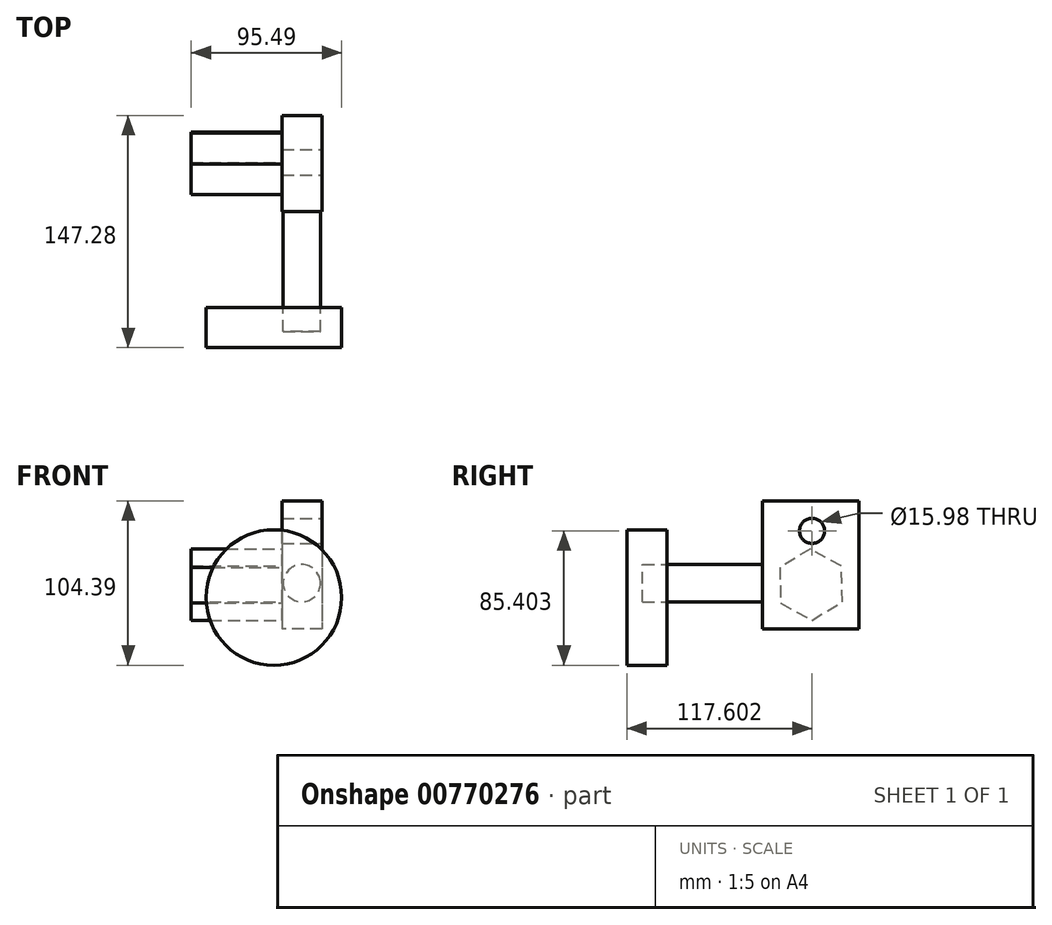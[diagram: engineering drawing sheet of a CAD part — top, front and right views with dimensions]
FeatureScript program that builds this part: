
annotation { "Feature Type Name" : "Feature", "Feature Type Description" : "" }
export const myFeature = defineFeature(function(context is Context, id is Id, definition is map)
    precondition{}
    {
        {
            var Q0;
            Q0=qCreatedBy(makeId("Front.planeOp"),FACE);
            var sketch = newSketch(context, id + "F0", { "sketchPlane" : qUnion([Q0])});
            skCircle(sketch, "E0", {"center": v(-5.26, 6.11) * mm, "radius": 43.06 * mm});
            skSolve(sketch);
        }
        {
            var Q0;
            Q0=makeQuery(id+"F0.imprint","IMPRINT",FACE,{"disambiguationData":[TD([[makeQuery(id+"F0.imprint","IMPRINT",EDGE,{"derivedFrom":sQuery(id+"F0.wireOp",EDGE,"E0")}),1.0]])]});
            extrude(context, id + "F1", {"entities" : qUnion([Q0]), "depth" : 25.4 * mm, "offsetDistance" : 25.4 * mm});
        }
        {
            var Q0;
            Q0=qCreatedBy(makeId("Right.planeOp"),FACE);
            var sketch = newSketch(context, id + "F2", { "sketchPlane" : qUnion([Q0])});
            skLineSegment(sketch, "E1.bottom", {"start": v(60.8, 67.44) * mm, "end": v(121.88, 67.44) * mm});
            skLineSegment(sketch, "E1.top", {"start": v(60.8, -13.97) * mm, "end": v(121.88, -13.97) * mm});
            skLineSegment(sketch, "E1.left", {"start": v(60.8, 67.44) * mm, "end": v(60.8, -13.97) * mm});
            skLineSegment(sketch, "E1.right", {"start": v(121.88, 67.44) * mm, "end": v(121.88, -13.97) * mm});
            skSolve(sketch);
        }
        {
            var Q0;
            Q0=makeQuery(id+"F2.imprint","IMPRINT",FACE,{"disambiguationData":[TD([[makeQuery(id+"F2.imprint","IMPRINT",EDGE,{"derivedFrom":sQuery(id+"F2.wireOp",EDGE,"E1.bottom")}),-1.0]])]});
            extrude(context, id + "F3", {"entities" : qUnion([Q0]), "depth" : 25.4 * mm, "offsetDistance" : 25.4 * mm});
        }
        {
            var Q0;
            Q0=makeQuery(id+"F3.opExtrude","SWEPT_FACE",FACE,{"disambiguationData":[OSD([sQuery(id+"F2.wireOp",EDGE,"E1.left")])]});
            var sketch = newSketch(context, id + "F4", { "sketchPlane" : qUnion([Q0])});
            skCircle(sketch, "E2", {"center": v(12.52, 15.25) * mm, "radius": 11.84 * mm});
            skSolve(sketch);
        }
        {
            var Q0;
            Q0=makeQuery(id+"F4.imprint","IMPRINT",FACE,{"disambiguationData":[TD([[makeQuery(id+"F4.imprint","IMPRINT",EDGE,{"derivedFrom":sQuery(id+"F4.wireOp",EDGE,"E2")}),1.0]])]});
            extrude(context, id + "F5", {"entities" : qUnion([Q0]), "depth" : 76.2 * mm, "offsetDistance" : 25.4 * mm});
        }
        {
            var Q0;
            Q0=makeQuery(id+"F3.opExtrude","CAP_FACE",FACE,{"disambiguationData":[OSD([sQuery(id+"F2.wireOp",EDGE,"E1.bottom"),sQuery(id+"F2.wireOp",EDGE,"E1.top"),sQuery(id+"F2.wireOp",EDGE,"E1.left"),sQuery(id+"F2.wireOp",EDGE,"E1.right")])],"isStart":false});
            var sketch = newSketch(context, id + "F6", { "sketchPlane" : qUnion([Q0])});
            skPoint(sketch, "E3", {"position": v(92.2, 48.45) * mm});
            skSolve(sketch);
        }
        {
            var Q0;
            Q0=sQuery(id+"F6.wireOp",VERTEX,"E3");
            var Q1;
            Q1=makeQuery(id+"F3.opExtrude","SWEPT_BODY",BODY,{"disambiguationData":[OSD([sQuery(id+"F2.wireOp",EDGE,"E1.bottom"),sQuery(id+"F2.wireOp",EDGE,"E1.top"),sQuery(id+"F2.wireOp",EDGE,"E1.left"),sQuery(id+"F2.wireOp",EDGE,"E1.right")])]});
            hole(context, id + "F7", {"style" : HoleStyle.SIMPLE, "endStyle" : HoleEndStyle.THROUGH, "holeDiameter" : 15.98 * mm, "majorDiameter" : 6.35 * mm, "isTappedThrough" : true, "tappedDepth" : 12.7 * mm, "tapClearance" : 3, "locations" : qUnion([Q0]), "scope" : qUnion([Q1])});
        }
        {
            var Q0;
            Q0=makeQuery(id+"F3.opExtrude","CAP_FACE",FACE,{"disambiguationData":[OSD([sQuery(id+"F2.wireOp",EDGE,"E1.bottom"),sQuery(id+"F2.wireOp",EDGE,"E1.top"),sQuery(id+"F2.wireOp",EDGE,"E1.left"),sQuery(id+"F2.wireOp",EDGE,"E1.right")])],"isStart":true});
            var sketch = newSketch(context, id + "F8", { "sketchPlane" : qUnion([Q0])});
            skCircle(sketch, "E4.cCircle", {"center": v(-91.55, 14.28) * mm, "radius": 19.6 * mm, "construction": true});
            skLineSegment(sketch, "E4.0", {"start": v(-91.05, 36.9) * mm, "end": v(-71.7, 25.16) * mm});
            skLineSegment(sketch, "E4.1", {"start": v(-71.7, 25.16) * mm, "end": v(-72.2, 2.54) * mm});
            skLineSegment(sketch, "E4.2", {"start": v(-72.2, 2.54) * mm, "end": v(-92.04, -8.34) * mm});
            skLineSegment(sketch, "E4.3", {"start": v(-92.04, -8.34) * mm, "end": v(-111.38, 3.4) * mm});
            skLineSegment(sketch, "E4.4", {"start": v(-111.38, 3.4) * mm, "end": v(-110.9, 26.02) * mm});
            skLineSegment(sketch, "E4.5", {"start": v(-110.9, 26.02) * mm, "end": v(-91.05, 36.9) * mm});
            skPoint(sketch, "E4.0.midPoint", {"position": v(-81.38, 31.03) * mm});
            skSolve(sketch);
        }
        {
            var Q0;
            Q0=makeQuery(id+"F8.imprint","IMPRINT",FACE,{"disambiguationData":[TD([[makeQuery(id+"F8.imprint","IMPRINT",EDGE,{"derivedFrom":sQuery(id+"F8.wireOp",EDGE,"E4.0")}),-1.0]])]});
            extrude(context, id + "F9", {"entities" : qUnion([Q0]), "operationType" : NewBodyOperationType.ADD, "depth" : 57.68 * mm, "offsetDistance" : 25.4 * mm});
        }
    });
